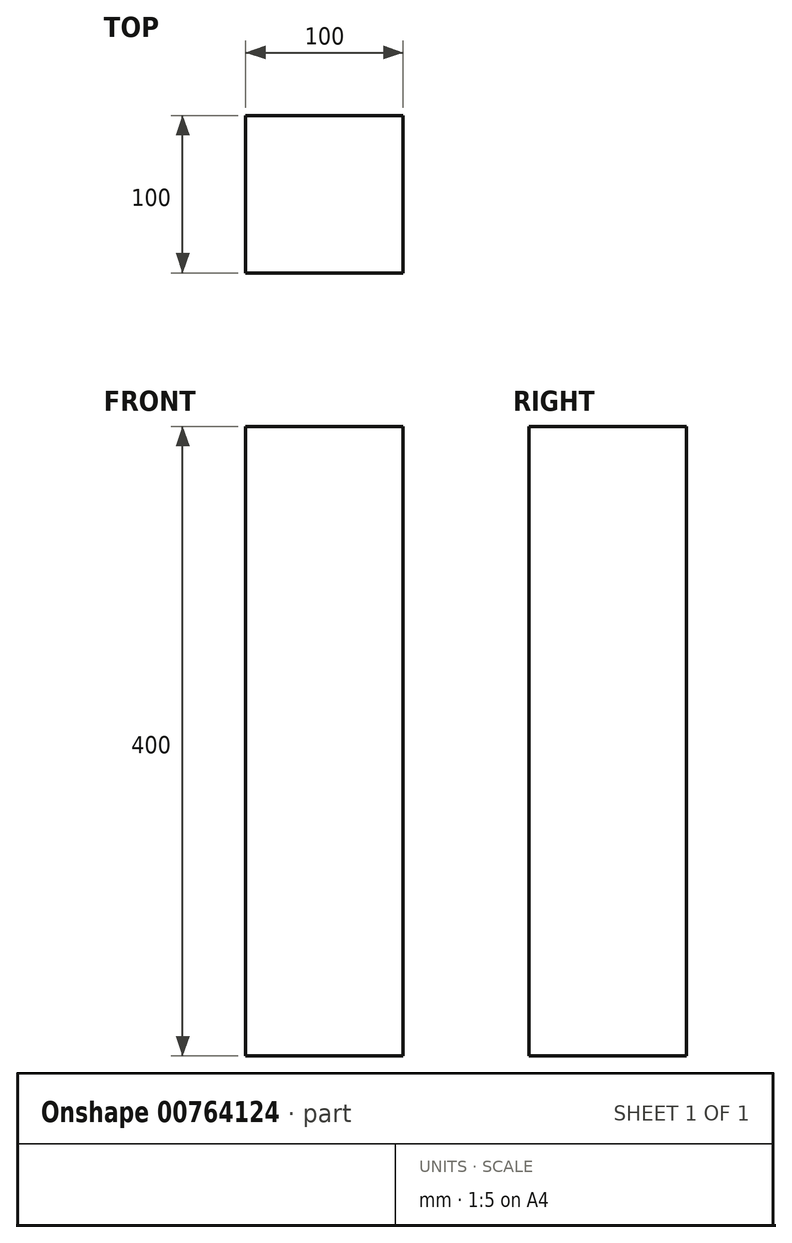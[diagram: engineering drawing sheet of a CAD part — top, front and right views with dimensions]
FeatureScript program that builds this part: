
annotation { "Feature Type Name" : "Feature", "Feature Type Description" : "" }
export const myFeature = defineFeature(function(context is Context, id is Id, definition is map)
    precondition{}
    {
        {
            var Q0;
            Q0=qCreatedBy(makeId("Top.planeOp"),FACE);
            var sketch = newSketch(context, id + "F0", { "sketchPlane" : qUnion([Q0])});
            skLineSegment(sketch, "E0.bottom", {"start": v(-50, 50) * mm, "end": v(50, 50) * mm});
            skLineSegment(sketch, "E0.top", {"start": v(-50, -50) * mm, "end": v(50, -50) * mm});
            skLineSegment(sketch, "E0.left", {"start": v(-50, 50) * mm, "end": v(-50, -50) * mm});
            skLineSegment(sketch, "E0.right", {"start": v(50, 50) * mm, "end": v(50, -50) * mm});
            skSolve(sketch);
        }
        {
            var Q0;
            Q0=makeQuery(id+"F0.imprint","IMPRINT",FACE,{"disambiguationData":[TD([[makeQuery(id+"F0.imprint","IMPRINT",EDGE,{"derivedFrom":sQuery(id+"F0.wireOp",EDGE,"E0.bottom")}),-1.0]])]});
            extrude(context, id + "F1", {"entities" : qUnion([Q0]), "depth" : 400 * mm, "offsetDistance" : 25 * mm});
        }
    });
